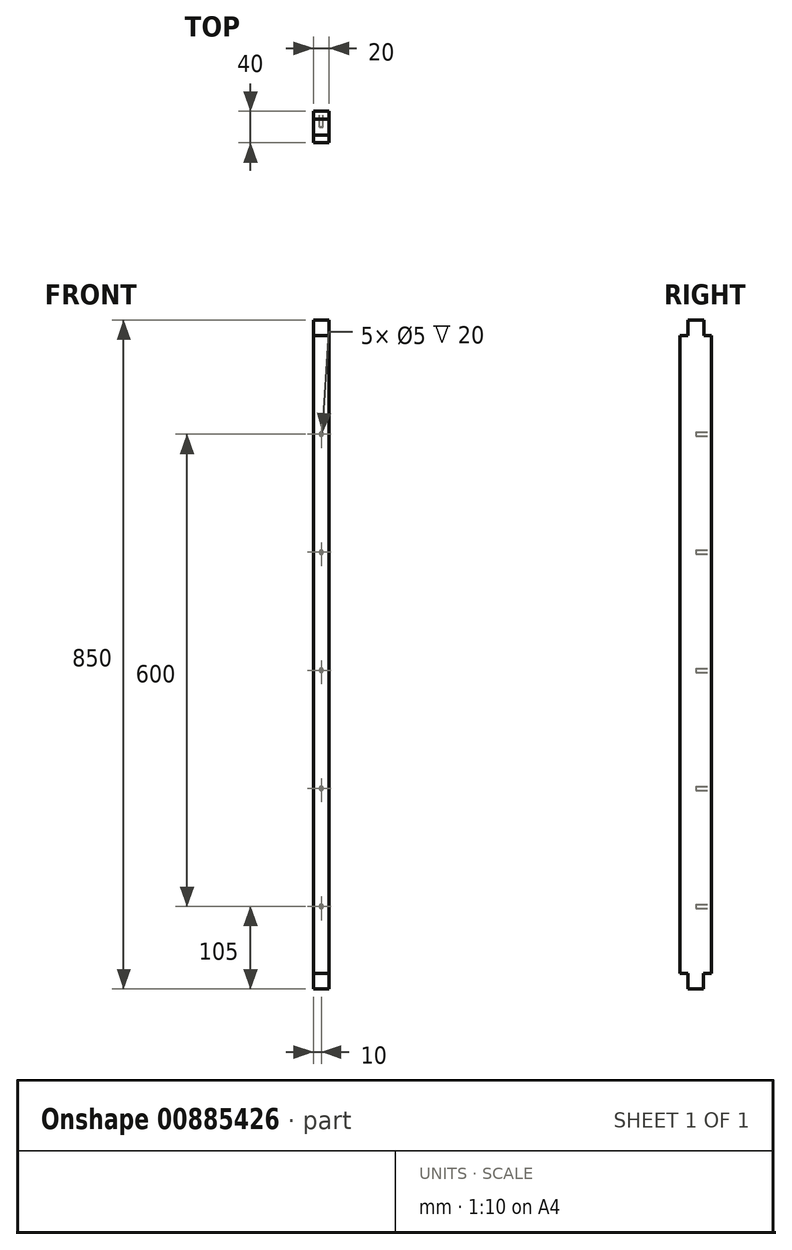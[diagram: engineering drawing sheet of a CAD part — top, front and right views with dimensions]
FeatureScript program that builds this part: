
annotation { "Feature Type Name" : "Feature", "Feature Type Description" : "" }
export const myFeature = defineFeature(function(context is Context, id is Id, definition is map)
    precondition{}
    {
        {
            var Q0;
            Q0=qCreatedBy(makeId("Top.planeOp"),FACE);
            var sketch = newSketch(context, id + "F0", { "sketchPlane" : qUnion([Q0])});
            skLineSegment(sketch, "E0.bottom", {"start": v(-10, 20) * mm, "end": v(10, 20) * mm});
            skLineSegment(sketch, "E0.top", {"start": v(-10, -20) * mm, "end": v(10, -20) * mm});
            skLineSegment(sketch, "E0.left", {"start": v(-10, 20) * mm, "end": v(-10, -20) * mm});
            skLineSegment(sketch, "E0.right", {"start": v(10, 20) * mm, "end": v(10, -20) * mm});
            skPoint(sketch, "E0.middle", {"position": v(0, 0) * mm});
            skSolve(sketch);
        }
        {
            var Q0;
            Q0=makeQuery(id+"F0.imprint","IMPRINT",FACE,{"disambiguationData":[TD([[makeQuery(id+"F0.imprint","IMPRINT",EDGE,{"derivedFrom":sQuery(id+"F0.wireOp",EDGE,"E0.bottom")}),-1.0]])]});
            extrude(context, id + "F1", {"entities" : qUnion([Q0]), "depth" : 850 * mm, "offsetDistance" : 25 * mm});
        }
        {
            var Q0;
            Q0=makeQuery(id+"F1.opExtrude","SWEPT_FACE",FACE,{"disambiguationData":[OSD([sQuery(id+"F0.wireOp",EDGE,"E0.bottom")])]});
            var sketch = newSketch(context, id + "F2", { "sketchPlane" : qUnion([Q0])});
            skCircle(sketch, "E1", {"center": v(0, 705) * mm, "radius": 2.5 * mm});
            skCircle(sketch, "E2", {"center": v(0, 555) * mm, "radius": 2.5 * mm});
            skCircle(sketch, "E3", {"center": v(0, 405) * mm, "radius": 2.5 * mm});
            skCircle(sketch, "E4", {"center": v(0, 255) * mm, "radius": 2.5 * mm});
            skCircle(sketch, "E5", {"center": v(0, 105) * mm, "radius": 2.5 * mm});
            skSolve(sketch);
        }
        {
            var Q0;
            Q0=makeQuery(id+"F2.imprint","IMPRINT",FACE,{"disambiguationData":[TD([[makeQuery(id+"F2.imprint","IMPRINT",EDGE,{"derivedFrom":sQuery(id+"F2.wireOp",EDGE,"E2")}),1.0]])]});
            var Q1;
            Q1=makeQuery(id+"F2.imprint","IMPRINT",FACE,{"disambiguationData":[TD([[makeQuery(id+"F2.imprint","IMPRINT",EDGE,{"derivedFrom":sQuery(id+"F2.wireOp",EDGE,"E1")}),1.0]])]});
            var Q2;
            Q2=makeQuery(id+"F2.imprint","IMPRINT",FACE,{"disambiguationData":[TD([[makeQuery(id+"F2.imprint","IMPRINT",EDGE,{"derivedFrom":sQuery(id+"F2.wireOp",EDGE,"E4")}),1.0]])]});
            var Q3;
            Q3=makeQuery(id+"F2.imprint","IMPRINT",FACE,{"disambiguationData":[TD([[makeQuery(id+"F2.imprint","IMPRINT",EDGE,{"derivedFrom":sQuery(id+"F2.wireOp",EDGE,"E5")}),1.0]])]});
            var Q4;
            Q4=makeQuery(id+"F2.imprint","IMPRINT",FACE,{"disambiguationData":[TD([[makeQuery(id+"F2.imprint","IMPRINT",EDGE,{"derivedFrom":sQuery(id+"F2.wireOp",EDGE,"E3")}),1.0]])]});
            extrude(context, id + "F3", {"entities" : qUnion([Q0, Q1, Q2, Q3, Q4]), "operationType" : NewBodyOperationType.REMOVE, "oppositeDirection" : true, "depth" : 20 * mm, "offsetDistance" : 25 * mm});
        }
        {
            var Q0;
            Q0=makeQuery(id+"F1.opExtrude","SWEPT_FACE",FACE,{"disambiguationData":[OSD([sQuery(id+"F0.wireOp",EDGE,"E0.right")])]});
            var sketch = newSketch(context, id + "F4", { "sketchPlane" : qUnion([Q0])});
            skLineSegment(sketch, "E6.bottom", {"start": v(-20, 0) * mm, "end": v(-10, 0) * mm});
            skLineSegment(sketch, "E6.top", {"start": v(-20, 20) * mm, "end": v(-10, 20) * mm});
            skLineSegment(sketch, "E6.left", {"start": v(-20, 0) * mm, "end": v(-20, 20) * mm});
            skLineSegment(sketch, "E6.right", {"start": v(-10, 0) * mm, "end": v(-10, 20) * mm});
            skLineSegment(sketch, "E7.bottom", {"start": v(20, 0) * mm, "end": v(9.65, 0) * mm});
            skLineSegment(sketch, "E7.top", {"start": v(20, 20) * mm, "end": v(9.65, 20) * mm});
            skLineSegment(sketch, "E7.left", {"start": v(20, 0) * mm, "end": v(20, 20) * mm});
            skLineSegment(sketch, "E7.right", {"start": v(9.65, 0) * mm, "end": v(9.65, 20) * mm});
            skLineSegment(sketch, "E8.bottom", {"start": v(-20, 850) * mm, "end": v(-10, 850) * mm});
            skLineSegment(sketch, "E8.top", {"start": v(-20, 830) * mm, "end": v(-10, 830) * mm});
            skLineSegment(sketch, "E8.left", {"start": v(-20, 850) * mm, "end": v(-20, 830) * mm});
            skLineSegment(sketch, "E8.right", {"start": v(-10, 850) * mm, "end": v(-10, 830) * mm});
            skLineSegment(sketch, "E9.bottom", {"start": v(20, 850) * mm, "end": v(10, 850) * mm});
            skLineSegment(sketch, "E9.top", {"start": v(20, 830) * mm, "end": v(10, 830) * mm});
            skLineSegment(sketch, "E9.left", {"start": v(20, 850) * mm, "end": v(20, 830) * mm});
            skLineSegment(sketch, "E9.right", {"start": v(10, 850) * mm, "end": v(10, 830) * mm});
            skSolve(sketch);
        }
        {
            var Q0;
            Q0=makeQuery(id+"F4.imprint","IMPRINT",FACE,{"disambiguationData":[TD([[makeQuery(id+"F4.imprint","IMPRINT",EDGE,{"derivedFrom":sQuery(id+"F4.wireOp",EDGE,"E8.bottom")}),1.0]])]});
            var Q1;
            Q1=makeQuery(id+"F4.imprint","IMPRINT",FACE,{"disambiguationData":[TD([[makeQuery(id+"F4.imprint","IMPRINT",EDGE,{"derivedFrom":sQuery(id+"F4.wireOp",EDGE,"E9.bottom")}),1.0]])]});
            var Q2;
            Q2=makeQuery(id+"F4.imprint","IMPRINT",FACE,{"disambiguationData":[TD([[makeQuery(id+"F4.imprint","IMPRINT",EDGE,{"derivedFrom":sQuery(id+"F4.wireOp",EDGE,"E7.bottom")}),-1.0]])]});
            var Q3;
            Q3=makeQuery(id+"F4.imprint","IMPRINT",FACE,{"disambiguationData":[TD([[makeQuery(id+"F4.imprint","IMPRINT",EDGE,{"derivedFrom":sQuery(id+"F4.wireOp",EDGE,"E6.bottom")}),-1.0]])]});
            extrude(context, id + "F5", {"entities" : qUnion([Q0, Q1, Q2, Q3]), "operationType" : NewBodyOperationType.REMOVE, "oppositeDirection" : true, "depth" : 500 * mm, "offsetDistance" : 25 * mm});
        }
    });
